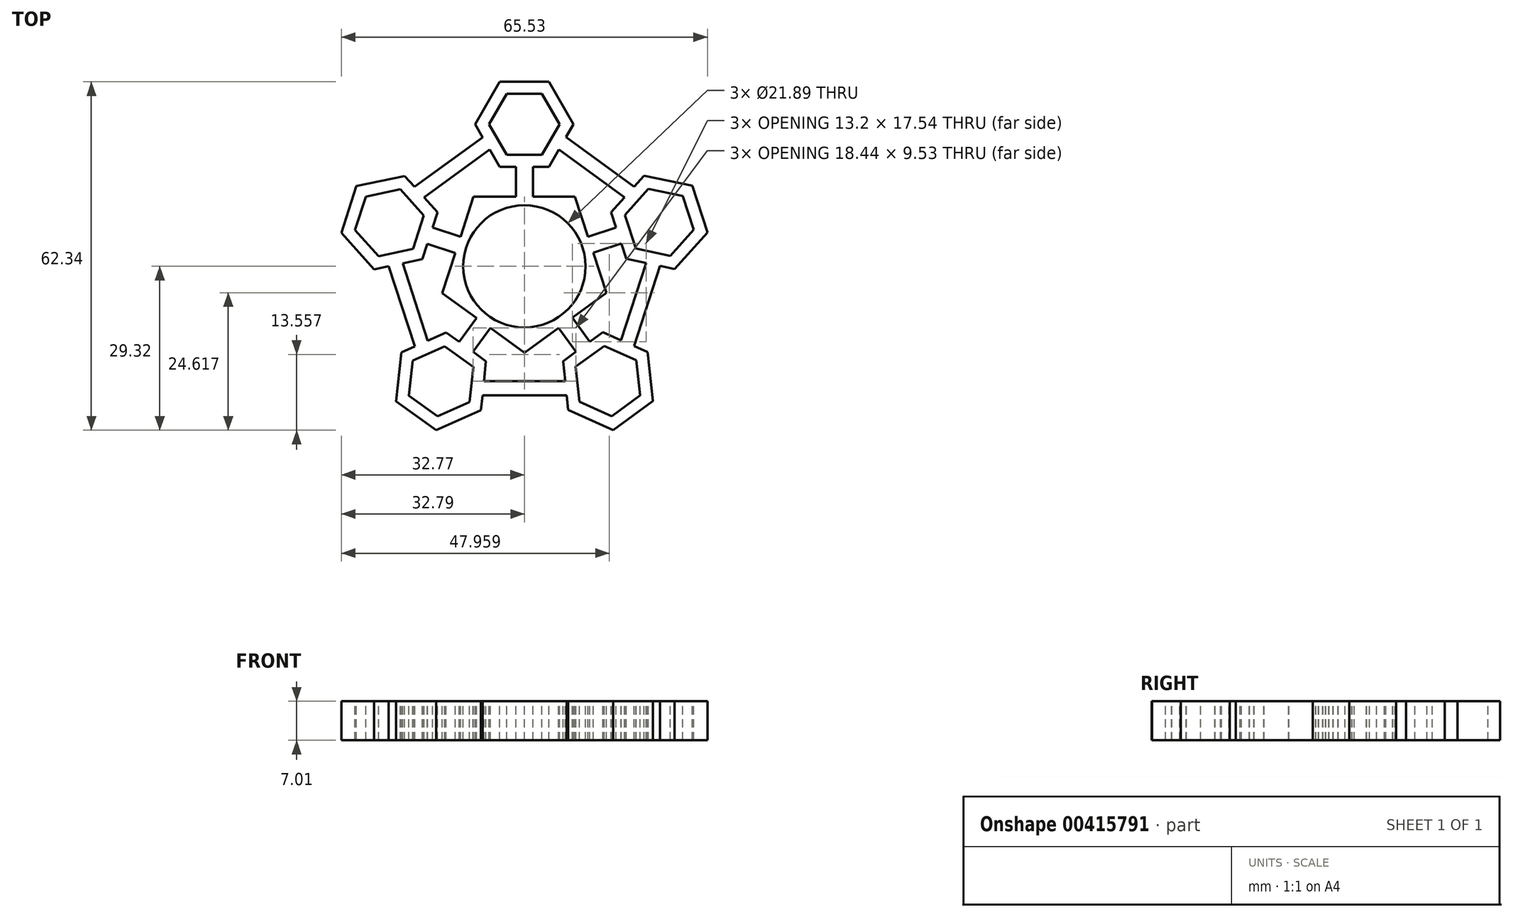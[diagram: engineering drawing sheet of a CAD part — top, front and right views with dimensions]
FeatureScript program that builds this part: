
annotation { "Feature Type Name" : "Feature", "Feature Type Description" : "" }
export const myFeature = defineFeature(function(context is Context, id is Id, definition is map)
    precondition{}
    {
        {
            var Q0;
            Q0=qCreatedBy(makeId("Top.planeOp"),FACE);
            var sketch = newSketch(context, id + "F0", { "sketchPlane" : qUnion([Q0])});
            skCircle(sketch, "E0", {"center": v(0, 0) * mm, "radius": 10.95 * mm});
            skCircle(sketch, "E1.cCircle", {"center": v(0, 0) * mm, "radius": 12.5 * mm, "construction": true});
            skLineSegment(sketch, "E1.0", {"start": v(-9.1, 12.48) * mm, "end": v(9.06, 12.5) * mm});
            skLineSegment(sketch, "E1.1", {"start": v(9.06, 12.5) * mm, "end": v(14.7, -4.75) * mm});
            skLineSegment(sketch, "E1.2", {"start": v(14.7, -4.75) * mm, "end": v(0.02, -15.44) * mm});
            skLineSegment(sketch, "E1.3", {"start": v(0.02, -15.44) * mm, "end": v(-14.68, -4.8) * mm});
            skLineSegment(sketch, "E1.4", {"start": v(-14.68, -4.8) * mm, "end": v(-9.1, 12.48) * mm});
            skLineSegment(sketch, "E2", {"start": v(0, 0) * mm, "end": v(0, 25.4) * mm});
            skLineSegment(sketch, "E3", {"start": v(0, 0) * mm, "end": v(-24.17, 7.82) * mm});
            skLineSegment(sketch, "E4", {"start": v(0, 0) * mm, "end": v(-14.9, -20.57) * mm});
            skLineSegment(sketch, "E5", {"start": v(0, 0) * mm, "end": v(14.96, -20.53) * mm});
            skLineSegment(sketch, "E6", {"start": v(0, 0) * mm, "end": v(24.15, 7.88) * mm});
            skCircle(sketch, "E7.cCircle", {"center": v(-24.17, 7.82) * mm, "radius": 5.46 * mm, "construction": true});
            skLineSegment(sketch, "E7.0", {"start": v(-18, 9.14) * mm, "end": v(-19.94, 3.14) * mm});
            skLineSegment(sketch, "E7.1", {"start": v(-19.94, 3.14) * mm, "end": v(-26.1, 1.82) * mm});
            skLineSegment(sketch, "E7.2", {"start": v(-26.1, 1.82) * mm, "end": v(-30.33, 6.5) * mm});
            skLineSegment(sketch, "E7.3", {"start": v(-30.33, 6.5) * mm, "end": v(-28.4, 12.5) * mm});
            skLineSegment(sketch, "E7.4", {"start": v(-28.4, 12.5) * mm, "end": v(-22.23, 13.82) * mm});
            skLineSegment(sketch, "E7.5", {"start": v(-22.23, 13.82) * mm, "end": v(-18, 9.14) * mm});
            skPoint(sketch, "E7.0.midPoint", {"position": v(-18.97, 6.14) * mm});
            skCircle(sketch, "E8.cCircle", {"center": v(24.15, 7.88) * mm, "radius": 5.46 * mm, "construction": true});
            skLineSegment(sketch, "E8.0", {"start": v(19.93, 3.19) * mm, "end": v(17.98, 9.18) * mm});
            skLineSegment(sketch, "E8.1", {"start": v(17.98, 9.18) * mm, "end": v(22.2, 13.87) * mm});
            skLineSegment(sketch, "E8.2", {"start": v(22.2, 13.87) * mm, "end": v(28.36, 12.57) * mm});
            skLineSegment(sketch, "E8.3", {"start": v(28.36, 12.57) * mm, "end": v(30.32, 6.58) * mm});
            skLineSegment(sketch, "E8.4", {"start": v(30.32, 6.58) * mm, "end": v(26.1, 1.89) * mm});
            skLineSegment(sketch, "E8.5", {"start": v(26.1, 1.89) * mm, "end": v(19.93, 3.19) * mm});
            skPoint(sketch, "E8.0.midPoint", {"position": v(18.96, 6.19) * mm});
            skCircle(sketch, "E9.cCircle", {"center": v(14.96, -20.53) * mm, "radius": 5.46 * mm, "construction": true});
            skLineSegment(sketch, "E9.0", {"start": v(9.2, -17.97) * mm, "end": v(14.29, -14.26) * mm});
            skLineSegment(sketch, "E9.1", {"start": v(14.29, -14.26) * mm, "end": v(20.05, -16.82) * mm});
            skLineSegment(sketch, "E9.2", {"start": v(20.05, -16.82) * mm, "end": v(20.72, -23.09) * mm});
            skLineSegment(sketch, "E9.3", {"start": v(20.72, -23.09) * mm, "end": v(15.62, -26.8) * mm});
            skLineSegment(sketch, "E9.4", {"start": v(15.62, -26.8) * mm, "end": v(9.86, -24.24) * mm});
            skLineSegment(sketch, "E9.5", {"start": v(9.86, -24.24) * mm, "end": v(9.2, -17.97) * mm});
            skPoint(sketch, "E9.0.midPoint", {"position": v(11.74, -16.12) * mm});
            skCircle(sketch, "E10.cCircle", {"center": v(-14.9, -20.57) * mm, "radius": 5.46 * mm, "construction": true});
            skLineSegment(sketch, "E10.0", {"start": v(-14.25, -14.3) * mm, "end": v(-9.15, -18) * mm});
            skLineSegment(sketch, "E10.1", {"start": v(-9.15, -18) * mm, "end": v(-9.8, -24.27) * mm});
            skLineSegment(sketch, "E10.2", {"start": v(-9.8, -24.27) * mm, "end": v(-15.55, -26.84) * mm});
            skLineSegment(sketch, "E10.3", {"start": v(-15.55, -26.84) * mm, "end": v(-20.66, -23.14) * mm});
            skLineSegment(sketch, "E10.4", {"start": v(-20.66, -23.14) * mm, "end": v(-20, -16.87) * mm});
            skLineSegment(sketch, "E10.5", {"start": v(-20, -16.87) * mm, "end": v(-14.25, -14.3) * mm});
            skPoint(sketch, "E10.0.midPoint", {"position": v(-11.7, -16.15) * mm});
            skCircle(sketch, "E11.cCircle", {"center": v(-24.17, 7.82) * mm, "radius": 7.62 * mm, "construction": true});
            skLineSegment(sketch, "E11.0", {"start": v(-15.56, 9.66) * mm, "end": v(-18.27, 1.29) * mm});
            skLineSegment(sketch, "E11.1", {"start": v(-18.27, 1.29) * mm, "end": v(-26.88, -0.55) * mm});
            skLineSegment(sketch, "E11.2", {"start": v(-26.88, -0.55) * mm, "end": v(-32.77, 5.98) * mm});
            skLineSegment(sketch, "E11.3", {"start": v(-32.77, 5.98) * mm, "end": v(-30.06, 14.35) * mm});
            skLineSegment(sketch, "E11.4", {"start": v(-30.06, 14.35) * mm, "end": v(-21.46, 16.19) * mm});
            skLineSegment(sketch, "E11.5", {"start": v(-21.46, 16.19) * mm, "end": v(-15.56, 9.66) * mm});
            skPoint(sketch, "E11.0.midPoint", {"position": v(-16.92, 5.47) * mm});
            skCircle(sketch, "E12.cCircle", {"center": v(24.15, 7.88) * mm, "radius": 7.62 * mm, "construction": true});
            skLineSegment(sketch, "E12.0", {"start": v(18.27, 1.33) * mm, "end": v(15.54, 9.7) * mm});
            skLineSegment(sketch, "E12.1", {"start": v(15.54, 9.7) * mm, "end": v(21.42, 16.24) * mm});
            skLineSegment(sketch, "E12.2", {"start": v(21.42, 16.24) * mm, "end": v(30.03, 14.43) * mm});
            skLineSegment(sketch, "E12.3", {"start": v(30.03, 14.43) * mm, "end": v(32.76, 6.06) * mm});
            skLineSegment(sketch, "E12.4", {"start": v(32.76, 6.06) * mm, "end": v(26.88, -0.48) * mm});
            skLineSegment(sketch, "E12.5", {"start": v(26.88, -0.48) * mm, "end": v(18.27, 1.33) * mm});
            skPoint(sketch, "E12.0.midPoint", {"position": v(16.9, 5.52) * mm});
            skCircle(sketch, "E13.cCircle", {"center": v(14.96, -20.53) * mm, "radius": 7.62 * mm, "construction": true});
            skLineSegment(sketch, "E13.0", {"start": v(6.91, -16.96) * mm, "end": v(14.03, -11.78) * mm});
            skLineSegment(sketch, "E13.1", {"start": v(14.03, -11.78) * mm, "end": v(22.07, -15.35) * mm});
            skLineSegment(sketch, "E13.2", {"start": v(22.07, -15.35) * mm, "end": v(23, -24.1) * mm});
            skLineSegment(sketch, "E13.3", {"start": v(23, -24.1) * mm, "end": v(15.89, -29.28) * mm});
            skLineSegment(sketch, "E13.4", {"start": v(15.89, -29.28) * mm, "end": v(7.84, -25.71) * mm});
            skLineSegment(sketch, "E13.5", {"start": v(7.84, -25.71) * mm, "end": v(6.91, -16.96) * mm});
            skPoint(sketch, "E13.0.midPoint", {"position": v(10.47, -14.37) * mm});
            skCircle(sketch, "E14.cCircle", {"center": v(-14.9, -20.57) * mm, "radius": 7.62 * mm, "construction": true});
            skLineSegment(sketch, "E14.0", {"start": v(-14, -11.82) * mm, "end": v(-6.87, -16.98) * mm});
            skLineSegment(sketch, "E14.1", {"start": v(-6.87, -16.98) * mm, "end": v(-7.78, -25.73) * mm});
            skLineSegment(sketch, "E14.2", {"start": v(-7.78, -25.73) * mm, "end": v(-15.81, -29.32) * mm});
            skLineSegment(sketch, "E14.3", {"start": v(-15.81, -29.32) * mm, "end": v(-22.94, -24.16) * mm});
            skLineSegment(sketch, "E14.4", {"start": v(-22.94, -24.16) * mm, "end": v(-22.03, -15.4) * mm});
            skLineSegment(sketch, "E14.5", {"start": v(-22.03, -15.4) * mm, "end": v(-14, -11.82) * mm});
            skPoint(sketch, "E14.0.midPoint", {"position": v(-10.43, -14.4) * mm});
            skLineSegment(sketch, "E15", {"start": v(-1.52, 17.78) * mm, "end": v(-1.52, 12.5) * mm});
            skLineSegment(sketch, "E16", {"start": v(1.52, 17.78) * mm, "end": v(1.52, 12.5) * mm});
            skLineSegment(sketch, "E17", {"start": v(16.43, 6.96) * mm, "end": v(11.32, 5.3) * mm});
            skLineSegment(sketch, "E18", {"start": v(12.35, 2.43) * mm, "end": v(17.38, 4.07) * mm});
            skLineSegment(sketch, "E19", {"start": v(8.59, -9.2) * mm, "end": v(11.8, -13.6) * mm});
            skLineSegment(sketch, "E20", {"start": v(6.13, -11) * mm, "end": v(9.33, -15.4) * mm});
            skLineSegment(sketch, "E21", {"start": v(-6.1, -11.01) * mm, "end": v(-9.2, -15.3) * mm});
            skLineSegment(sketch, "E22", {"start": v(-8.57, -9.22) * mm, "end": v(-11.67, -13.5) * mm});
            skLineSegment(sketch, "E23", {"start": v(-12.36, 2.4) * mm, "end": v(-17.39, 4.02) * mm});
            skPoint(sketch, "E24.endSnap0", {"position": v(-12.08, 3.9) * mm});
            skLineSegment(sketch, "E25", {"start": v(-16.45, 6.92) * mm, "end": v(-11.42, 5.3) * mm});
            skLineSegment(sketch, "E26", {"start": v(-24.17, 7.82) * mm, "end": v(-14.9, -20.57) * mm});
            skLineSegment(sketch, "E27", {"start": v(-14.9, -20.53) * mm, "end": v(14.96, -20.53) * mm});
            skLineSegment(sketch, "E28", {"start": v(14.96, -20.53) * mm, "end": v(24.15, 7.88) * mm});
            skLineSegment(sketch, "E29", {"start": v(24.15, 7.88) * mm, "end": v(0, 25.4) * mm});
            skLineSegment(sketch, "E30", {"start": v(0, 25.4) * mm, "end": v(-24.17, 7.82) * mm});
            skLineSegment(sketch, "E31", {"start": v(-24.29, 0) * mm, "end": v(-19.61, -14.33) * mm});
            skLineSegment(sketch, "E32", {"start": v(-19.3, 1.07) * mm, "end": v(-14.95, -12.24) * mm});
            skLineSegment(sketch, "E33", {"start": v(-6.97, -17.99) * mm, "end": v(7.02, -17.99) * mm});
            skLineSegment(sketch, "E34", {"start": v(-7.5, -23.07) * mm, "end": v(7.56, -23.07) * mm});
            skLineSegment(sketch, "E35", {"start": v(14.98, -12.2) * mm, "end": v(19.29, 1.12) * mm});
            skLineSegment(sketch, "E36", {"start": v(24.29, 0.06) * mm, "end": v(19.65, -14.28) * mm});
            skLineSegment(sketch, "E37", {"start": v(19.65, 14.28) * mm, "end": v(7.45, 23.13) * mm});
            skLineSegment(sketch, "E38", {"start": v(4.9, 18.7) * mm, "end": v(16.24, 10.48) * mm});
            skLineSegment(sketch, "E39", {"start": v(-7.5, 23.09) * mm, "end": v(-19.68, 14.22) * mm});
            skLineSegment(sketch, "E40", {"start": v(-16.26, 10.43) * mm, "end": v(-4.94, 18.67) * mm});
            skPoint(sketch, "E41.0.midPoint", {"position": v(4.9, 18.7) * mm});
            skPoint(sketch, "E42.0.midPoint", {"position": v(-3.03, 23.2) * mm});
            skPoint(sketch, "E43.0.midPoint", {"position": v(2.99, 23.23) * mm});
            skPoint(sketch, "E44.cCircle.perimeterSnap0", {"position": v(-8.05, 25.46) * mm});
            skPoint(sketch, "E44.0.midPoint", {"position": v(-8.05, 26.3) * mm});
            skPoint(sketch, "E44.0.midPoint.positionSnap0", {"position": v(-8.05, 25.46) * mm});
            skPoint(sketch, "E45.cCircle.perimeterSnap0", {"position": v(8.05, 25.46) * mm});
            skPoint(sketch, "E45.0.midPoint", {"position": v(8.05, 26.3) * mm});
            skPoint(sketch, "E45.0.midPoint.positionSnap0", {"position": v(8.05, 25.46) * mm});
            skLineSegment(sketch, "E46", {"start": v(-14.1, 18.29) * mm, "end": v(-19.68, 14.22) * mm});
            skLineSegment(sketch, "E47", {"start": v(-16.26, 10.43) * mm, "end": v(-11.05, 14.22) * mm});
            skLineSegment(sketch, "E48", {"start": v(-11.05, 14.22) * mm, "end": v(-16.26, 10.43) * mm});
            skCircle(sketch, "E49.cCircle", {"center": v(0, 25.4) * mm, "radius": 7.62 * mm, "construction": true});
            skLineSegment(sketch, "E49.0", {"start": v(4.4, 17.78) * mm, "end": v(-4.4, 17.78) * mm});
            skLineSegment(sketch, "E49.1", {"start": v(-4.4, 17.78) * mm, "end": v(-8.8, 25.4) * mm});
            skLineSegment(sketch, "E49.2", {"start": v(-8.8, 25.4) * mm, "end": v(-4.4, 33.02) * mm});
            skLineSegment(sketch, "E49.3", {"start": v(-4.4, 33.02) * mm, "end": v(4.4, 33.02) * mm});
            skLineSegment(sketch, "E49.4", {"start": v(4.4, 33.02) * mm, "end": v(8.8, 25.4) * mm});
            skLineSegment(sketch, "E49.5", {"start": v(8.8, 25.4) * mm, "end": v(4.4, 17.78) * mm});
            skPoint(sketch, "E49.0.midPoint", {"position": v(0, 17.78) * mm});
            skCircle(sketch, "E50.cCircle", {"center": v(0, 25.4) * mm, "radius": 5.46 * mm, "construction": true});
            skLineSegment(sketch, "E50.0", {"start": v(3.15, 19.94) * mm, "end": v(-3.15, 19.94) * mm});
            skLineSegment(sketch, "E50.1", {"start": v(-3.15, 19.94) * mm, "end": v(-6.3, 25.4) * mm});
            skLineSegment(sketch, "E50.2", {"start": v(-6.3, 25.4) * mm, "end": v(-3.15, 30.86) * mm});
            skLineSegment(sketch, "E50.3", {"start": v(-3.15, 30.86) * mm, "end": v(3.15, 30.86) * mm});
            skLineSegment(sketch, "E50.4", {"start": v(3.15, 30.86) * mm, "end": v(6.3, 25.4) * mm});
            skLineSegment(sketch, "E50.5", {"start": v(6.3, 25.4) * mm, "end": v(3.15, 19.94) * mm});
            skPoint(sketch, "E50.0.midPoint", {"position": v(0, 19.94) * mm});
            skLineSegment(sketch, "E51", {"start": v(-7.5, 23.09) * mm, "end": v(-7.57, 23.04) * mm});
            skLineSegment(sketch, "E52", {"start": v(-7.57, 23.04) * mm, "end": v(-7.47, 23.1) * mm});
            skSolve(sketch);
        }
        {
            var Q0;
            {var subQ0=sQuery(id+"F0.wireOp",EDGE,"E31");Q0=makeQuery(id+"F0.imprint","IMPRINT",FACE,{"disambiguationData":[TD([[makeQuery(id+"F0.imprint","IMPRINT",EDGE,{"derivedFrom":subQ0}),1.0]])]});}
            var Q1;
            {var subQ1=sQuery(id+"F0.wireOp",EDGE,"E39");Q1=makeQuery(id+"F0.imprint","IMPRINT",FACE,{"disambiguationData":[TD([[makeQuery(id+"F0.imprint","IMPRINT",EDGE,{"derivedFrom":subQ1}),1.0]])]});}
            var Q2;
            {var subQ0=sQuery(id+"F0.wireOp",EDGE,"E37");Q2=makeQuery(id+"F0.imprint","IMPRINT",FACE,{"disambiguationData":[TD([[makeQuery(id+"F0.imprint","IMPRINT",EDGE,{"derivedFrom":subQ0}),1.0]])]});}
            var Q3;
            {var subQ0=sQuery(id+"F0.wireOp",EDGE,"E36");Q3=makeQuery(id+"F0.imprint","IMPRINT",FACE,{"disambiguationData":[TD([[makeQuery(id+"F0.imprint","IMPRINT",EDGE,{"derivedFrom":subQ0}),-1.0]])]});}
            var Q4;
            {var subQ0=sQuery(id+"F0.wireOp",EDGE,"E34");Q4=makeQuery(id+"F0.imprint","IMPRINT",FACE,{"disambiguationData":[TD([[makeQuery(id+"F0.imprint","IMPRINT",EDGE,{"derivedFrom":subQ0}),1.0]])]});}
            var Q5;
            {var subQ0=sQuery(id+"F0.wireOp",EDGE,"E37");Q5=makeQuery(id+"F0.imprint","IMPRINT",FACE,{"disambiguationData":[TD([[makeQuery(id+"F0.imprint","IMPRINT",EDGE,{"derivedFrom":subQ0}),1.0]])]});}
            var Q6;
            {var subQ1=sQuery(id+"F0.wireOp",EDGE,"E39");Q6=makeQuery(id+"F0.imprint","IMPRINT",FACE,{"disambiguationData":[TD([[makeQuery(id+"F0.imprint","IMPRINT",EDGE,{"derivedFrom":subQ1}),1.0]])]});}
            var Q7;
            {var subQ0=sQuery(id+"F0.wireOp",EDGE,"E16");Q7=makeQuery(id+"F0.imprint","IMPRINT",FACE,{"disambiguationData":[TD([[makeQuery(id+"F0.imprint","IMPRINT",EDGE,{"derivedFrom":subQ0}),-1.0]])]});}
            var Q8;
            {var subQ10=sQuery(id+"F0.wireOp",EDGE,"E7.2");Q8=makeQuery(id+"F0.imprint","IMPRINT",FACE,{"disambiguationData":[TD([[makeQuery(id+"F0.imprint","IMPRINT",EDGE,{"derivedFrom":subQ10}),1.0]])]});}
            var Q9;
            {var subQ7=sQuery(id+"F0.wireOp",EDGE,"E8.2");Q9=makeQuery(id+"F0.imprint","IMPRINT",FACE,{"disambiguationData":[TD([[makeQuery(id+"F0.imprint","IMPRINT",EDGE,{"derivedFrom":subQ7}),1.0]])]});}
            var Q10;
            {var subQ12=sQuery(id+"F0.wireOp",EDGE,"E9.2");Q10=makeQuery(id+"F0.imprint","IMPRINT",FACE,{"disambiguationData":[TD([[makeQuery(id+"F0.imprint","IMPRINT",EDGE,{"derivedFrom":subQ12}),1.0]])]});}
            var Q11;
            {var subQ11=sQuery(id+"F0.wireOp",EDGE,"E10.2");Q11=makeQuery(id+"F0.imprint","IMPRINT",FACE,{"disambiguationData":[TD([[makeQuery(id+"F0.imprint","IMPRINT",EDGE,{"derivedFrom":subQ11}),1.0]])]});}
            var Q12;
            {var subQ0=sQuery(id+"F0.wireOp",EDGE,"E31");Q12=makeQuery(id+"F0.imprint","IMPRINT",FACE,{"disambiguationData":[TD([[makeQuery(id+"F0.imprint","IMPRINT",EDGE,{"derivedFrom":subQ0}),1.0]])]});}
            var Q13;
            {var subQ1=sQuery(id+"F0.wireOp",EDGE,"E39");Q13=makeQuery(id+"F0.imprint","IMPRINT",FACE,{"disambiguationData":[TD([[makeQuery(id+"F0.imprint","IMPRINT",EDGE,{"derivedFrom":subQ1}),1.0]])]});}
            var Q14;
            {var subQ0=sQuery(id+"F0.wireOp",EDGE,"E37");Q14=makeQuery(id+"F0.imprint","IMPRINT",FACE,{"disambiguationData":[TD([[makeQuery(id+"F0.imprint","IMPRINT",EDGE,{"derivedFrom":subQ0}),1.0]])]});}
            var Q15;
            {var subQ0=sQuery(id+"F0.wireOp",EDGE,"E36");Q15=makeQuery(id+"F0.imprint","IMPRINT",FACE,{"disambiguationData":[TD([[makeQuery(id+"F0.imprint","IMPRINT",EDGE,{"derivedFrom":subQ0}),-1.0]])]});}
            var Q16;
            {var subQ0=sQuery(id+"F0.wireOp",EDGE,"E34");Q16=makeQuery(id+"F0.imprint","IMPRINT",FACE,{"disambiguationData":[TD([[makeQuery(id+"F0.imprint","IMPRINT",EDGE,{"derivedFrom":subQ0}),1.0]])]});}
            var Q17;
            {var subQ0=sQuery(id+"F0.wireOp",EDGE,"E37");Q17=makeQuery(id+"F0.imprint","IMPRINT",FACE,{"disambiguationData":[TD([[makeQuery(id+"F0.imprint","IMPRINT",EDGE,{"derivedFrom":subQ0}),1.0]])]});}
            var Q18;
            {var subQ1=sQuery(id+"F0.wireOp",EDGE,"E39");Q18=makeQuery(id+"F0.imprint","IMPRINT",FACE,{"disambiguationData":[TD([[makeQuery(id+"F0.imprint","IMPRINT",EDGE,{"derivedFrom":subQ1}),1.0]])]});}
            var Q19;
            {var subQ0=sQuery(id+"F0.wireOp",EDGE,"E16");Q19=makeQuery(id+"F0.imprint","IMPRINT",FACE,{"disambiguationData":[TD([[makeQuery(id+"F0.imprint","IMPRINT",EDGE,{"derivedFrom":subQ0}),-1.0]])]});}
            var Q20;
            {var subQ10=sQuery(id+"F0.wireOp",EDGE,"E7.2");Q20=makeQuery(id+"F0.imprint","IMPRINT",FACE,{"disambiguationData":[TD([[makeQuery(id+"F0.imprint","IMPRINT",EDGE,{"derivedFrom":subQ10}),1.0]])]});}
            var Q21;
            {var subQ7=sQuery(id+"F0.wireOp",EDGE,"E8.2");Q21=makeQuery(id+"F0.imprint","IMPRINT",FACE,{"disambiguationData":[TD([[makeQuery(id+"F0.imprint","IMPRINT",EDGE,{"derivedFrom":subQ7}),1.0]])]});}
            var Q22;
            {var subQ12=sQuery(id+"F0.wireOp",EDGE,"E9.2");Q22=makeQuery(id+"F0.imprint","IMPRINT",FACE,{"disambiguationData":[TD([[makeQuery(id+"F0.imprint","IMPRINT",EDGE,{"derivedFrom":subQ12}),1.0]])]});}
            var Q23;
            {var subQ11=sQuery(id+"F0.wireOp",EDGE,"E10.2");Q23=makeQuery(id+"F0.imprint","IMPRINT",FACE,{"disambiguationData":[TD([[makeQuery(id+"F0.imprint","IMPRINT",EDGE,{"derivedFrom":subQ11}),1.0]])]});}
            var Q24;
            {var subQ1=sQuery(id+"F0.wireOp",EDGE,"E11.0");var subQ7=sQuery(id+"F0.wireOp",EDGE,"E3");var subQ12=makeQuery(id+"F0.imprint","INTERSECT",VERTEX,{"derivedFrom":[subQ7,subQ1]});Q24=makeQuery(id+"F0.imprint","IMPRINT",FACE,{"disambiguationData":[TD([[makeQuery(id+"F0.imprint","IMPRINT",EDGE,{"disambiguationData":[TD([[subQ12,-1.0]])],"derivedFrom":subQ7}),-1.0]])]});}
            var Q25;
            {var subQ5=sQuery(id+"F0.wireOp",EDGE,"E3");var subQ7=sQuery(id+"F0.wireOp",EDGE,"E11.0");var subQ9=makeQuery(id+"F0.imprint","INTERSECT",VERTEX,{"derivedFrom":[subQ5,subQ7]});Q25=makeQuery(id+"F0.imprint","IMPRINT",FACE,{"disambiguationData":[TD([[makeQuery(id+"F0.imprint","IMPRINT",EDGE,{"disambiguationData":[TD([[subQ9,-1.0]])],"derivedFrom":subQ5}),1.0]])]});}
            var Q26;
            {var subQ1=sQuery(id+"F0.wireOp",EDGE,"E14.0");var subQ9=sQuery(id+"F0.wireOp",EDGE,"E4");var subQ11=makeQuery(id+"F0.imprint","INTERSECT",VERTEX,{"derivedFrom":[subQ9,subQ1]});Q26=makeQuery(id+"F0.imprint","IMPRINT",FACE,{"disambiguationData":[TD([[makeQuery(id+"F0.imprint","IMPRINT",EDGE,{"disambiguationData":[TD([[subQ11,-1.0]])],"derivedFrom":subQ9}),-1.0]])]});}
            var Q27;
            {var subQ0=sQuery(id+"F0.wireOp",EDGE,"E21");Q27=makeQuery(id+"F0.imprint","IMPRINT",FACE,{"disambiguationData":[TD([[makeQuery(id+"F0.imprint","IMPRINT",EDGE,{"derivedFrom":subQ0}),-1.0]])]});}
            var Q28;
            {var subQ0=sQuery(id+"F0.wireOp",EDGE,"E22");Q28=makeQuery(id+"F0.imprint","IMPRINT",FACE,{"disambiguationData":[TD([[makeQuery(id+"F0.imprint","IMPRINT",EDGE,{"derivedFrom":subQ0}),1.0]])]});}
            var Q29;
            {var subQ6=sQuery(id+"F0.wireOp",EDGE,"E14.0");var subQ9=sQuery(id+"F0.wireOp",EDGE,"E4");var subQ10=makeQuery(id+"F0.imprint","INTERSECT",VERTEX,{"derivedFrom":[subQ9,subQ6]});Q29=makeQuery(id+"F0.imprint","IMPRINT",FACE,{"disambiguationData":[TD([[makeQuery(id+"F0.imprint","IMPRINT",EDGE,{"disambiguationData":[TD([[subQ10,-1.0]])],"derivedFrom":subQ9}),1.0]])]});}
            var Q30;
            {var subQ1=sQuery(id+"F0.wireOp",EDGE,"E13.0");var subQ9=sQuery(id+"F0.wireOp",EDGE,"E5");var subQ10=makeQuery(id+"F0.imprint","INTERSECT",VERTEX,{"derivedFrom":[subQ9,subQ1]});Q30=makeQuery(id+"F0.imprint","IMPRINT",FACE,{"disambiguationData":[TD([[makeQuery(id+"F0.imprint","IMPRINT",EDGE,{"disambiguationData":[TD([[subQ10,-1.0]])],"derivedFrom":subQ9}),-1.0]])]});}
            var Q31;
            {var subQ5=sQuery(id+"F0.wireOp",EDGE,"E5");var subQ7=sQuery(id+"F0.wireOp",EDGE,"E13.0");var subQ9=makeQuery(id+"F0.imprint","INTERSECT",VERTEX,{"derivedFrom":[subQ5,subQ7]});Q31=makeQuery(id+"F0.imprint","IMPRINT",FACE,{"disambiguationData":[TD([[makeQuery(id+"F0.imprint","IMPRINT",EDGE,{"disambiguationData":[TD([[subQ9,-1.0]])],"derivedFrom":subQ5}),1.0]])]});}
            var Q32;
            {var subQ0=sQuery(id+"F0.wireOp",EDGE,"E19");var subQ1=sQuery(id+"F0.wireOp",EDGE,"E1.2");var subQ2=makeQuery(id+"F0.imprint","INTERSECT",VERTEX,{"derivedFrom":[subQ1,subQ0]});Q32=makeQuery(id+"F0.imprint","IMPRINT",FACE,{"disambiguationData":[TD([[makeQuery(id+"F0.imprint","IMPRINT",EDGE,{"disambiguationData":[TD([[subQ2,-1.0]])],"derivedFrom":subQ1}),1.0]])]});}
            var Q33;
            {var subQ0=sQuery(id+"F0.wireOp",EDGE,"E20");var subQ1=sQuery(id+"F0.wireOp",EDGE,"E1.2");var subQ2=makeQuery(id+"F0.imprint","INTERSECT",VERTEX,{"derivedFrom":[subQ1,subQ0]});Q33=makeQuery(id+"F0.imprint","IMPRINT",FACE,{"disambiguationData":[TD([[makeQuery(id+"F0.imprint","IMPRINT",EDGE,{"disambiguationData":[TD([[subQ2,1.0]])],"derivedFrom":subQ1}),1.0]])]});}
            var Q34;
            {var subQ4=sQuery(id+"F0.wireOp",EDGE,"E6");var subQ5=sQuery(id+"F0.wireOp",EDGE,"E0");var subQ6=makeQuery(id+"F0.imprint","INTERSECT",VERTEX,{"derivedFrom":[subQ5,subQ4]});Q34=makeQuery(id+"F0.imprint","IMPRINT",FACE,{"disambiguationData":[TD([[makeQuery(id+"F0.imprint","IMPRINT",EDGE,{"disambiguationData":[TD([[subQ6,1.0]])],"derivedFrom":subQ5}),-1.0]])]});}
            var Q35;
            {var subQ7=sQuery(id+"F0.wireOp",EDGE,"E4");var subQ8=sQuery(id+"F0.wireOp",EDGE,"E0");var subQ9=makeQuery(id+"F0.imprint","INTERSECT",VERTEX,{"derivedFrom":[subQ8,subQ7]});Q35=makeQuery(id+"F0.imprint","IMPRINT",FACE,{"disambiguationData":[TD([[makeQuery(id+"F0.imprint","IMPRINT",EDGE,{"disambiguationData":[TD([[subQ9,-1.0]])],"derivedFrom":subQ8}),-1.0]])]});}
            var Q36;
            {var subQ5=sQuery(id+"F0.wireOp",EDGE,"E3");var subQ6=sQuery(id+"F0.wireOp",EDGE,"E0");var subQ7=makeQuery(id+"F0.imprint","INTERSECT",VERTEX,{"derivedFrom":[subQ6,subQ5]});Q36=makeQuery(id+"F0.imprint","IMPRINT",FACE,{"disambiguationData":[TD([[makeQuery(id+"F0.imprint","IMPRINT",EDGE,{"disambiguationData":[TD([[subQ7,-1.0]])],"derivedFrom":subQ6}),-1.0]])]});}
            var Q37;
            {var subQ4=sQuery(id+"F0.wireOp",EDGE,"E2");var subQ5=sQuery(id+"F0.wireOp",EDGE,"E0");var subQ6=makeQuery(id+"F0.imprint","INTERSECT",VERTEX,{"derivedFrom":[subQ5,subQ4]});Q37=makeQuery(id+"F0.imprint","IMPRINT",FACE,{"disambiguationData":[TD([[makeQuery(id+"F0.imprint","IMPRINT",EDGE,{"disambiguationData":[TD([[subQ6,-1.0]])],"derivedFrom":subQ5}),-1.0]])]});}
            var Q38;
            {var subQ5=sQuery(id+"F0.wireOp",EDGE,"E2");var subQ7=sQuery(id+"F0.wireOp",EDGE,"E0");var subQ8=makeQuery(id+"F0.imprint","INTERSECT",VERTEX,{"derivedFrom":[subQ7,subQ5]});Q38=makeQuery(id+"F0.imprint","IMPRINT",FACE,{"disambiguationData":[TD([[makeQuery(id+"F0.imprint","IMPRINT",EDGE,{"disambiguationData":[TD([[subQ8,1.0]])],"derivedFrom":subQ7}),-1.0]])]});}
            var Q39;
            {var subQ0=sQuery(id+"F0.wireOp",EDGE,"E16");Q39=makeQuery(id+"F0.imprint","IMPRINT",FACE,{"disambiguationData":[TD([[makeQuery(id+"F0.imprint","IMPRINT",EDGE,{"derivedFrom":subQ0}),-1.0]])]});}
            var Q40;
            {var subQ0=sQuery(id+"F0.wireOp",EDGE,"E16");Q40=makeQuery(id+"F0.imprint","IMPRINT",FACE,{"disambiguationData":[TD([[makeQuery(id+"F0.imprint","IMPRINT",EDGE,{"derivedFrom":subQ0}),-1.0]])]});}
            var Q41;
            {var subQ0=sQuery(id+"F0.wireOp",EDGE,"E25");Q41=makeQuery(id+"F0.imprint","IMPRINT",FACE,{"disambiguationData":[TD([[makeQuery(id+"F0.imprint","IMPRINT",EDGE,{"derivedFrom":subQ0}),-1.0]])]});}
            var Q42;
            {var subQ0=sQuery(id+"F0.wireOp",EDGE,"E23");Q42=makeQuery(id+"F0.imprint","IMPRINT",FACE,{"disambiguationData":[TD([[makeQuery(id+"F0.imprint","IMPRINT",EDGE,{"derivedFrom":subQ0}),-1.0]])]});}
            var Q43;
            {var subQ0=sQuery(id+"F0.wireOp",EDGE,"E17");var subQ1=sQuery(id+"F0.wireOp",EDGE,"E1.1");var subQ2=makeQuery(id+"F0.imprint","INTERSECT",VERTEX,{"derivedFrom":[subQ1,subQ0]});Q43=makeQuery(id+"F0.imprint","IMPRINT",FACE,{"disambiguationData":[TD([[makeQuery(id+"F0.imprint","IMPRINT",EDGE,{"disambiguationData":[TD([[subQ2,-1.0]])],"derivedFrom":subQ1}),1.0]])]});}
            var Q44;
            {var subQ0=sQuery(id+"F0.wireOp",EDGE,"E18");Q44=makeQuery(id+"F0.imprint","IMPRINT",FACE,{"disambiguationData":[TD([[makeQuery(id+"F0.imprint","IMPRINT",EDGE,{"derivedFrom":subQ0}),1.0]])]});}
            var Q45;
            {var subQ6=sQuery(id+"F0.wireOp",EDGE,"E12.0");var subQ9=sQuery(id+"F0.wireOp",EDGE,"E6");var subQ12=makeQuery(id+"F0.imprint","INTERSECT",VERTEX,{"derivedFrom":[subQ9,subQ6]});Q45=makeQuery(id+"F0.imprint","IMPRINT",FACE,{"disambiguationData":[TD([[makeQuery(id+"F0.imprint","IMPRINT",EDGE,{"disambiguationData":[TD([[subQ12,-1.0]])],"derivedFrom":subQ9}),1.0]])]});}
            var Q46;
            {var subQ1=sQuery(id+"F0.wireOp",EDGE,"E12.0");var subQ9=sQuery(id+"F0.wireOp",EDGE,"E6");var subQ11=makeQuery(id+"F0.imprint","INTERSECT",VERTEX,{"derivedFrom":[subQ9,subQ1]});Q46=makeQuery(id+"F0.imprint","IMPRINT",FACE,{"disambiguationData":[TD([[makeQuery(id+"F0.imprint","IMPRINT",EDGE,{"disambiguationData":[TD([[subQ11,-1.0]])],"derivedFrom":subQ9}),-1.0]])]});}
            var Q47;
            {var subQ0=sQuery(id+"F0.wireOp",EDGE,"E15");Q47=makeQuery(id+"F0.imprint","IMPRINT",FACE,{"disambiguationData":[TD([[makeQuery(id+"F0.imprint","IMPRINT",EDGE,{"derivedFrom":subQ0}),1.0]])]});}
            var Q48;
            {var subQ0=sQuery(id+"F0.wireOp",EDGE,"E49.0");var subQ2=sQuery(id+"F0.wireOp",EDGE,"E2");var subQ3=makeQuery(id+"F0.imprint","INTERSECT",VERTEX,{"derivedFrom":[subQ2,subQ0]});Q48=makeQuery(id+"F0.imprint","IMPRINT",FACE,{"disambiguationData":[TD([[makeQuery(id+"F0.imprint","IMPRINT",EDGE,{"disambiguationData":[TD([[subQ3,-1.0]])],"derivedFrom":subQ2}),-1.0]])]});}
            var Q49;
            {var subQ0=sQuery(id+"F0.wireOp",EDGE,"E49.0");var subQ4=sQuery(id+"F0.wireOp",EDGE,"E2");var subQ5=makeQuery(id+"F0.imprint","INTERSECT",VERTEX,{"derivedFrom":[subQ4,subQ0]});Q49=makeQuery(id+"F0.imprint","IMPRINT",FACE,{"disambiguationData":[TD([[makeQuery(id+"F0.imprint","IMPRINT",EDGE,{"disambiguationData":[TD([[subQ5,-1.0]])],"derivedFrom":subQ4}),1.0]])]});}
            var Q50;
            {var subQ11=sQuery(id+"F0.wireOp",EDGE,"E49.2");Q50=makeQuery(id+"F0.imprint","IMPRINT",FACE,{"disambiguationData":[TD([[makeQuery(id+"F0.imprint","IMPRINT",EDGE,{"derivedFrom":subQ11}),-1.0]])]});}
            extrude(context, id + "F1", {"entities" : qUnion([Q0, Q1, Q2, Q3, Q4, Q5, Q6, Q7, Q8, Q9, Q10, Q11, Q12, Q13, Q14, Q15, Q16, Q17, Q18, Q19, Q20, Q21, Q22, Q23, Q24, Q25, Q26, Q27, Q28, Q29, Q30, Q31, Q32, Q33, Q34, Q35, Q36, Q37, Q38, Q39, Q40, Q41, Q42, Q43, Q44, Q45, Q46, Q47, Q48, Q49, Q50]), "oppositeDirection" : true, "depth" : 7 * mm});
        }
    });
